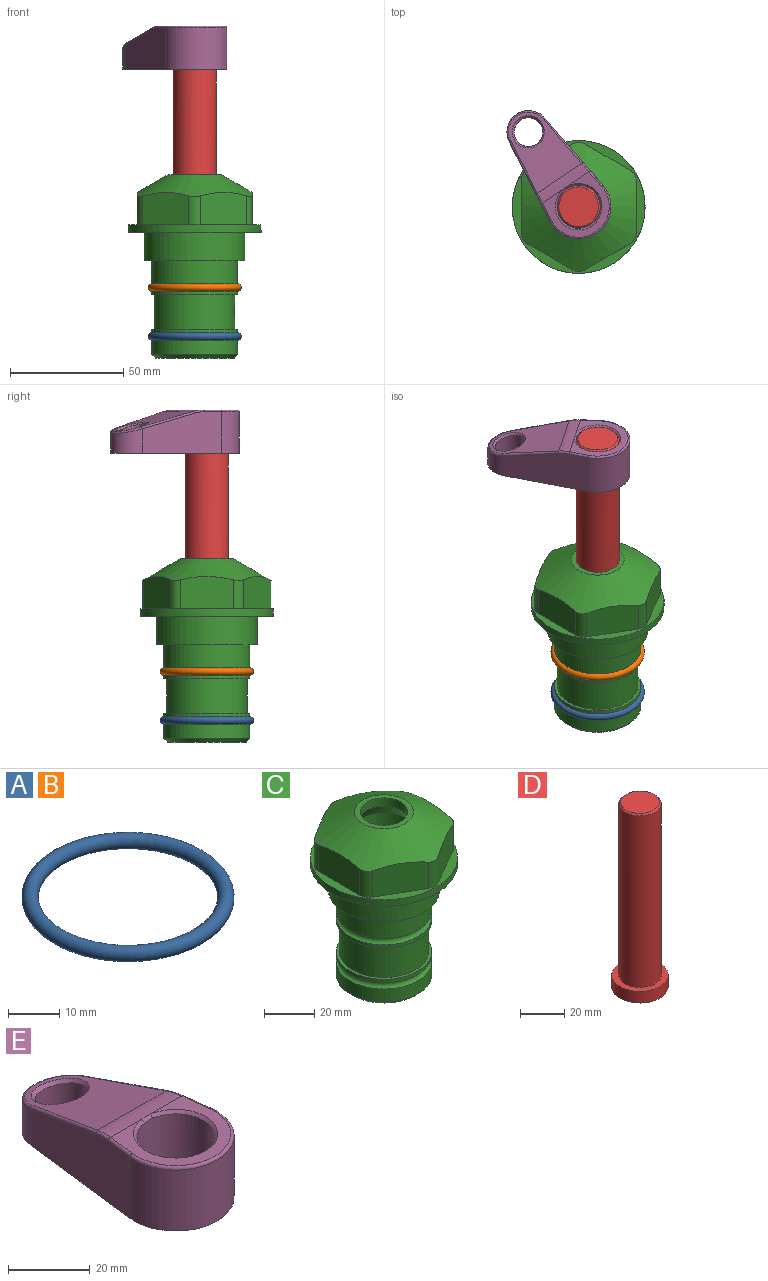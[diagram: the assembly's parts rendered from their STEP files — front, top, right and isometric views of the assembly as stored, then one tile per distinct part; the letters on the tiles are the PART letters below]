
ASSEMBLY  parts=5 mates=4
PART A: 1 faces, bbox 44.7x44.7x3.2 mm
  f0: torus R=19.05mm, axis (0,0,1), area 1193.9mm2
PART B: same geometry as A
PART C: 36 faces, bbox 58.7x58.7x81 mm
  f0: cylinder r=17.78mm len=35.56mm, axis (0,0,1), area 1670.8mm2, adj f23,f24,f31
  f1: cylinder r=19.05mm len=38.1mm, axis (0,0,1), area 1191.9mm2, adj f26,f27,f30
  f2: plane 58.66x58.66mm, normal (0,0,-1), area 1150.6mm2, adj f3,f28
  f3: cylinder r=29.33mm len=58.66mm, axis (0,0,-1), area 585.1mm2, adj f2,f4
  f4: plane 58.66x58.66mm, normal (0,0,1), area 475.9mm2, adj f3,f5,f6,f7,f8,f9,f10,f11
  f5: plane 20.32x14.34mm, normal (-0.5,0.87,0), area 324.4mm2, adj f4,f15,f16,f17
  f6: plane 20.32x14.34mm, normal (0.5,0.87,0), area 324.4mm2, adj f4,f14,f15,f17
  f7: plane 23.48x14.34mm, normal (1,0,0), area 324.4mm2, adj f4,f13,f14,f17
  f8: plane 20.32x14.34mm, normal (0.5,-0.87,0), area 324.4mm2, adj f4,f12,f13,f17
  f9: plane 20.32x14.34mm, normal (-0.5,-0.87,0), area 324.4mm2, adj f4,f11,f12,f17
  f10: plane 23.48x14.34mm, normal (-1,0,0), area 324.4mm2, adj f4,f11,f16,f17
  f11: cylinder r=5.08mm len=12.85mm, axis (0,0,-1), area 67.2mm2, adj f4,f9,f10,f17
  f12: cylinder r=5.08mm len=12.85mm, axis (0,0,-1), area 67.2mm2, adj f4,f8,f9,f17
  f13: cylinder r=5.08mm len=12.85mm, axis (0,0,-1), area 67.2mm2, adj f4,f7,f8,f17
  f14: cylinder r=5.08mm len=12.85mm, axis (0,0,-1), area 67.2mm2, adj f4,f6,f7,f17
  f15: cylinder r=5.08mm len=12.85mm, axis (0,0,-1), area 67.2mm2, adj f4,f5,f6,f17
  f16: cylinder r=5.08mm len=12.85mm, axis (0,0,-1), area 67.2mm2, adj f4,f5,f10,f17
  f17: cone r=11.73mm half-angle=60deg, axis (0,0,-1), area 2071.8mm2, adj f5,f6,f7,f8,f9,f10,f11,f12
  f18: plane 23.46x23.46mm, normal (0,0,1), area 147.4mm2, adj f17,f35
  f19: plane 34.93x34.93mm, normal (0,0,-1), area 958mm2, adj f29
  f20: cylinder r=19.05mm len=38.1mm, axis (0,0,1), area 760.1mm2, adj f21,f29
  f21: torus R=19.05mm, axis (0,0,1), area 565.3mm2, adj f20,f22
  f22: cylinder r=19.05mm len=38.1mm, axis (0,0,1), area 190mm2, adj f21,f23
  f23: plane 38.1x38.1mm, normal (0,0,1), area 146.9mm2, adj f0,f22
  f24: plane 38.1x38.1mm, normal (0,0,-1), area 146.9mm2, adj f0,f25
  f25: cylinder r=19.05mm len=38.1mm, axis (0,0,1), area 190mm2, adj f24,f26
  f26: torus R=19.05mm, axis (0,0,1), area 565.3mm2, adj f1,f25
  f27: plane 44.45x44.45mm, normal (0,0,-1), area 411.7mm2, adj f1,f28
  f28: cylinder r=22.23mm len=44.45mm, axis (0,0,1), area 1773.5mm2, adj f2,f27
  f29: cone r=19.05mm half-angle=45deg, axis (0,0,1), area 257.5mm2, adj f19,f20
  f30: cylinder r=3.17mm len=6.75mm, axis (-1,0,0), area 128mm2, adj f1,f33
  f31: cylinder r=3.17mm len=6.35mm, axis (-1,0,0), area 102.5mm2, adj f0,f33
  f32: plane 25.4x25.4mm, normal (0,0,1), area 506.7mm2, adj f33
  f33: cylinder r=12.7mm len=66.42mm, axis (0,0,-1), area 5236.2mm2, adj f30,f31,f32,f34
  f34: cone r=9.53mm half-angle=30deg, axis (0,0,-1), area 443.4mm2, adj f33,f35
  f35: cylinder r=9.53mm len=19.05mm, axis (0,0,-1), area 240.9mm2, adj f18,f34
PART D: 6 faces, bbox 25.4x25.4x101.6 mm
  f0: plane 17.46x17.46mm, normal (0,0,1), area 239.5mm2, adj f5
  f1: plane 25.4x25.4mm, normal (0,0,-1), area 506.7mm2, adj f2
  f2: cylinder r=12.7mm len=25.4mm, axis (0,0,1), area 506.7mm2, adj f1,f3
  f3: plane 25.4x25.4mm, normal (0,0,1), area 221.7mm2, adj f2,f4
  f4: cylinder r=9.53mm len=94.46mm, axis (0,0,1), area 5653mm2, adj f3,f5
  f5: cone r=8.73mm half-angle=45deg, axis (0,0,-1), area 64.4mm2, adj f0,f4
PART E: 31 faces, bbox 31.7x65.5x19.8 mm
  f0: plane 39.12x18.26mm, normal (0.99,0.12,0), area 612.2mm2, adj f1,f4,f7,f11,f13,f15
  f1: cylinder r=9.53mm len=18.91mm, axis (0,0,-1), area 296.1mm2, adj f0,f2,f7,f17
  f2: plane 39.12x18.26mm, normal (-0.99,0.12,0), area 612.2mm2, adj f1,f4,f7,f12,f14,f16
  f3: cylinder r=6.35mm len=12.7mm, axis (0,0,-1), area 362.4mm2, adj f7,f18
  f4: cylinder r=14.29mm len=28.58mm, axis (0,0,-1), area 882.2mm2, adj f0,f2,f7,f10
  f5: cylinder r=9.53mm len=19.05mm, axis (0,0,-1), area 1092.6mm2, adj f7,f19,f20
  f6: plane 26.99x23.69mm, normal (0,0,1), area 216.2mm2, adj f9,f10,f11,f12,f19
  f7: plane 63.5x28.58mm, normal (0,0,-1), area 661.8mm2, adj f0,f1,f2,f3,f4,f5,f22,f23
  f8: plane 33.52x23.6mm, normal (0,0.26,0.97), area 486mm2, adj f9,f15,f16,f17,f18
  f9: cylinder r=19.05mm len=24.72mm, axis (1,0,0), area 120.4mm2, adj f6,f8,f13,f14,f20
  f10: torus R=13.49mm, axis (0,0,1), area 59mm2, adj f4,f6,f11,f12
  f11: cylinder r=0.79mm len=8.67mm, axis (0.12,-0.99,0), area 10.8mm2, adj f0,f6,f10,f13
  f12: cylinder r=0.79mm len=8.67mm, axis (0.12,0.99,0), area 10.8mm2, adj f2,f6,f10,f14
  f13: bspline ~4.95x1.42mm, area 6.1mm2, adj f0,f9,f11,f15
  f14: bspline ~4.95x1.42mm, area 6.1mm2, adj f2,f9,f12,f16
  f15: cylinder r=0.79mm len=25.95mm, axis (0.12,-0.96,0.26), area 32.9mm2, adj f0,f8,f13,f17
  f16: cylinder r=0.79mm len=25.95mm, axis (0.12,0.96,-0.26), area 32.9mm2, adj f2,f8,f14,f17
  f17: bspline ~18.91x8.38mm, area 30mm2, adj f1,f8,f15,f16
  f18: bspline ~14.29x14.29mm, area 48.3mm2, adj f3,f8
  f19: cone r=9.53mm half-angle=45deg, axis (0,0,1), area 66.5mm2, adj f5,f6,f20
  f20: bspline ~3.22x0.96mm, area 3.5mm2, adj f5,f9,f19
  f21: plane 2.75x2.72mm, normal (0,0,-1), area 2.9mm2, adj f23,f25,f28
  f22: plane 23.05x15.88mm, normal (-0.99,-0.12,0), area 323.6mm2, adj f7,f25,f26,f27,f28,f29
  f23: plane 23.05x15.88mm, normal (0.99,-0.12,0), area 323.6mm2, adj f7,f21,f25,f27,f28,f30
  f24: cylinder r=9.53mm len=10.69mm, axis (0,0,-1), area 114.7mm2, adj f7,f27,f29,f30
  f25: cylinder r=12.7mm len=20.59mm, axis (0,0,-1), area 381.1mm2, adj f7,f21,f22,f23,f26,f28
  f26: plane 2.75x2.72mm, normal (0,0,-1), area 2.9mm2, adj f22,f25,f28
  f27: plane 19.72x18.37mm, normal (0,-0.26,-0.97), area 291.8mm2, adj f22,f23,f24,f28,f29,f30
  f28: cylinder r=15.88mm len=19.92mm, axis (1,0,0), area 54.8mm2, adj f21,f22,f23,f25,f26,f27
  f29: cylinder r=1.59mm len=11mm, axis (0,0,-1), area 34.7mm2, adj f7,f22,f24,f27
  f30: cylinder r=1.59mm len=11mm, axis (0,0,-1), area 34.7mm2, adj f7,f23,f24,f27
PLACE A t=(0,0,-21.59)mm
PLACE B at identity
PLACE C at identity fixed
PLACE D rot(axis=(0,0,1),33.9deg) t=(0,0,27.55)mm
PLACE E rot(axis=(0,0,1),33.9deg) t=(0,0,27.55)mm
MATE cylindrical D.f2 <-> C.f0  axis (0,0,-1) through (0,0,-10.55)mm
MATE fastened A.f0 <-> C.f0  axis (0,0,1) through (0,0,-46.1)mm
MATE fastened B.f0 <-> C.f0  axis (0,0,1) through (0,0,-24.51)mm
MATE fastened D.f2 <-> E.f4  axis (0,0,1) through (0,0,91.05)mm
